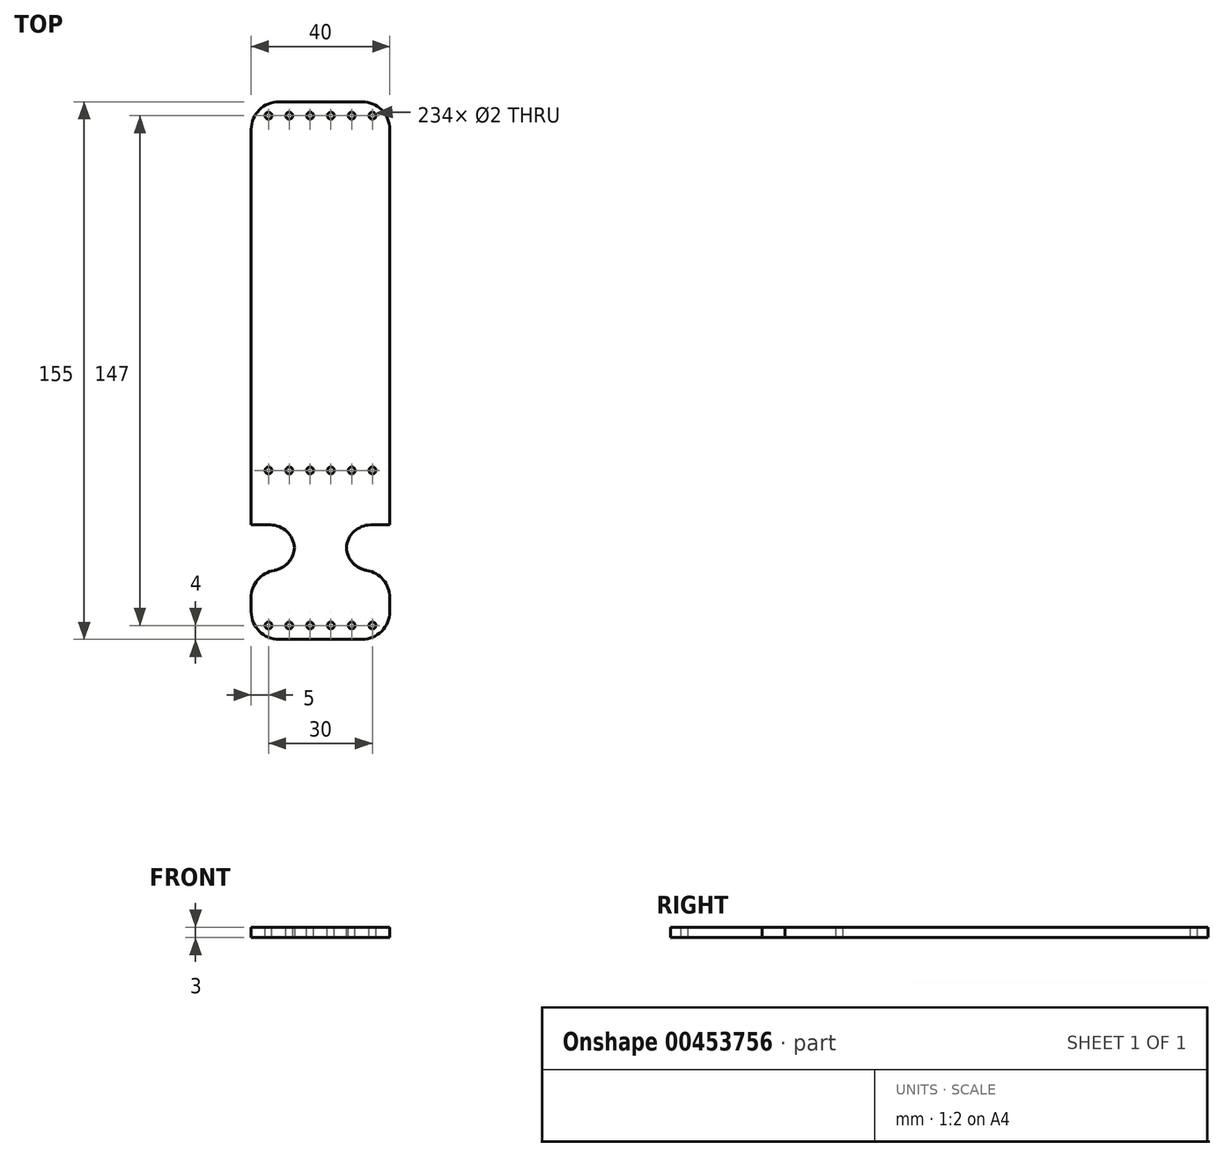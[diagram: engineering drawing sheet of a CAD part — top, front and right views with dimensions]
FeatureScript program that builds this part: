
annotation { "Feature Type Name" : "Feature", "Feature Type Description" : "" }
export const myFeature = defineFeature(function(context is Context, id is Id, definition is map)
    precondition{}
    {
        {
            var Q0;
            Q0=qCreatedBy(makeId("Top.planeOp"),FACE);
            var sketch = newSketch(context, id + "F0", { "sketchPlane" : qUnion([Q0])});
            skLineSegment(sketch, "E0.bottom", {"start": v(-20, 77.5) * mm, "end": v(20, 77.5) * mm});
            skLineSegment(sketch, "E0.top", {"start": v(-20, -77.5) * mm, "end": v(20, -77.5) * mm});
            skLineSegment(sketch, "E0.left", {"start": v(-20, 77.5) * mm, "end": v(-20, -77.5) * mm});
            skLineSegment(sketch, "E0.right", {"start": v(20, 77.5) * mm, "end": v(20, -77.5) * mm});
            skSolve(sketch);
        }
        {
            var Q0;
            Q0 = qSketchRegion(id + "F0", true);
            extrude(context, id + "F1", {"entities" : qUnion([Q0]), "depth" : 3 * mm});
        }
        {
            var Q0;
            Q0=makeQuery(id+"F1.opExtrude","CAP_FACE",FACE,{"disambiguationData":[OSD([sQuery(id+"F0.wireOp",EDGE,"E0.bottom"),sQuery(id+"F0.wireOp",EDGE,"E0.top"),sQuery(id+"F0.wireOp",EDGE,"E0.left"),sQuery(id+"F0.wireOp",EDGE,"E0.right")])],"isStart":false});
            var sketch = newSketch(context, id + "F2", { "sketchPlane" : qUnion([Q0])});
            skLineSegment(sketch, "E1.bottom", {"start": v(-20, -57.5) * mm, "end": v(20, -57.5) * mm});
            skLineSegment(sketch, "E1.top", {"start": v(-20, -44.5) * mm, "end": v(20, -44.5) * mm});
            skLineSegment(sketch, "E1.left", {"start": v(-20, -57.5) * mm, "end": v(-20, -44.5) * mm});
            skLineSegment(sketch, "E1.right", {"start": v(20, -57.5) * mm, "end": v(20, -44.5) * mm});
            skLineSegment(sketch, "E2.bottom", {"start": v(-7.5, -44.5) * mm, "end": v(7.5, -44.5) * mm});
            skLineSegment(sketch, "E2.top", {"start": v(-7.5, -57.5) * mm, "end": v(7.5, -57.5) * mm});
            skLineSegment(sketch, "E2.left", {"start": v(-7.5, -44.5) * mm, "end": v(-7.5, -57.5) * mm});
            skLineSegment(sketch, "E2.right", {"start": v(7.5, -44.5) * mm, "end": v(7.5, -57.5) * mm});
            skSolve(sketch);
        }
        {
            var Q0;
            {var subQ0=sQuery(id+"F2.wireOp",EDGE,"E1.left");Q0=makeQuery(id+"F2.imprint","IMPRINT",FACE,{"disambiguationData":[TD([[makeQuery(id+"F2.imprint","IMPRINT",EDGE,{"derivedFrom":subQ0}),1.0]])]});}
            var Q1;
            {var subQ0=sQuery(id+"F2.wireOp",EDGE,"E1.right");Q1=makeQuery(id+"F2.imprint","IMPRINT",FACE,{"disambiguationData":[TD([[makeQuery(id+"F2.imprint","IMPRINT",EDGE,{"derivedFrom":subQ0}),-1.0]])]});}
            extrude(context, id + "F3", {"entities" : qUnion([Q0, Q1]), "operationType" : NewBodyOperationType.REMOVE, "endBound" : BoundingType.UP_TO_NEXT, "oppositeDirection" : true, "depth" : 25 * mm});
        }
        {
            var Q0;
            Q0=makeQuery(id+"F3.boolean.opBoolean","COPY",EDGE,{"derivedFrom":makeQuery(id+"F3.opExtrude","SWEPT_EDGE",EDGE,{"disambiguationData":[OSD([sQuery(id+"F0.wireOp",EDGE,"E0.left"),sQuery(id+"F2.wireOp",EDGE,"E1.top"),sQuery(id+"F2.wireOp",EDGE,"E1.left")])]})});
            var Q1;
            Q1=makeQuery(id+"F3.boolean.opBoolean","COPY",EDGE,{"derivedFrom":makeQuery(id+"F3.opExtrude","SWEPT_EDGE",EDGE,{"disambiguationData":[OSD([sQuery(id+"F0.wireOp",EDGE,"E0.right"),sQuery(id+"F2.wireOp",EDGE,"E1.top"),sQuery(id+"F2.wireOp",EDGE,"E1.right")])]})});
            var Q2;
            Q2=makeQuery(id+"F3.boolean.opBoolean","COPY",EDGE,{"derivedFrom":makeQuery(id+"F3.opExtrude","SWEPT_EDGE",EDGE,{"disambiguationData":[OSD([sQuery(id+"F0.wireOp",EDGE,"E0.right"),sQuery(id+"F2.wireOp",EDGE,"E1.bottom"),sQuery(id+"F2.wireOp",EDGE,"E1.right")])]})});
            var Q3;
            Q3=makeQuery(id+"F3.boolean.opBoolean","COPY",EDGE,{"derivedFrom":makeQuery(id+"F3.opExtrude","SWEPT_EDGE",EDGE,{"disambiguationData":[OSD([sQuery(id+"F0.wireOp",EDGE,"E0.left"),sQuery(id+"F2.wireOp",EDGE,"E1.bottom"),sQuery(id+"F2.wireOp",EDGE,"E1.left")])]})});
            var Q4;
            Q4=makeQuery(id+"F1.opExtrude","SWEPT_EDGE",EDGE,{"disambiguationData":[OSD([sQuery(id+"F0.wireOp",EDGE,"E0.top"),sQuery(id+"F0.wireOp",EDGE,"E0.left")])]});
            var Q5;
            Q5=makeQuery(id+"F1.opExtrude","SWEPT_EDGE",EDGE,{"disambiguationData":[OSD([sQuery(id+"F0.wireOp",EDGE,"E0.top"),sQuery(id+"F0.wireOp",EDGE,"E0.right")])]});
            var Q6;
            Q6=makeQuery(id+"F1.opExtrude","SWEPT_EDGE",EDGE,{"disambiguationData":[OSD([sQuery(id+"F0.wireOp",EDGE,"E0.bottom"),sQuery(id+"F0.wireOp",EDGE,"E0.left")])]});
            var Q7;
            Q7=makeQuery(id+"F1.opExtrude","SWEPT_EDGE",EDGE,{"disambiguationData":[OSD([sQuery(id+"F0.wireOp",EDGE,"E0.bottom"),sQuery(id+"F0.wireOp",EDGE,"E0.right")])]});
            fillet(context, id + "F4", {"entities" : qUnion([Q0, Q1, Q2, Q3, Q4, Q5, Q6, Q7]), "radius" : 8 * mm, "tangentPropagation" : true, "allowEdgeOverflow" : false});
        }
        {
            var Q0;
            Q0=makeQuery(id+"F3.boolean.opBoolean","COPY",EDGE,{"derivedFrom":makeQuery(id+"F3.opExtrude","SWEPT_EDGE",EDGE,{"disambiguationData":[OSD([sQuery(id+"F2.wireOp",EDGE,"E1.top"),sQuery(id+"F2.wireOp",EDGE,"E2.bottom"),sQuery(id+"F2.wireOp",EDGE,"E2.left")])]})});
            var Q1;
            Q1=makeQuery(id+"F3.boolean.opBoolean","COPY",EDGE,{"derivedFrom":makeQuery(id+"F3.opExtrude","SWEPT_EDGE",EDGE,{"disambiguationData":[OSD([sQuery(id+"F2.wireOp",EDGE,"E1.bottom"),sQuery(id+"F2.wireOp",EDGE,"E2.top"),sQuery(id+"F2.wireOp",EDGE,"E2.left")])]})});
            var Q2;
            Q2=makeQuery(id+"F3.boolean.opBoolean","COPY",EDGE,{"derivedFrom":makeQuery(id+"F3.opExtrude","SWEPT_EDGE",EDGE,{"disambiguationData":[OSD([sQuery(id+"F2.wireOp",EDGE,"E1.top"),sQuery(id+"F2.wireOp",EDGE,"E2.bottom"),sQuery(id+"F2.wireOp",EDGE,"E2.right")])]})});
            var Q3;
            Q3=makeQuery(id+"F3.boolean.opBoolean","COPY",EDGE,{"derivedFrom":makeQuery(id+"F3.opExtrude","SWEPT_EDGE",EDGE,{"disambiguationData":[OSD([sQuery(id+"F2.wireOp",EDGE,"E1.bottom"),sQuery(id+"F2.wireOp",EDGE,"E2.top"),sQuery(id+"F2.wireOp",EDGE,"E2.right")])]})});
            fillet(context, id + "F5", {"entities" : qUnion([Q0, Q1, Q2, Q3]), "radius" : 7 * mm, "tangentPropagation" : true, "allowEdgeOverflow" : false});
        }
        {
            var Q0;
            Q0=makeQuery(id+"F1.opExtrude","CAP_FACE",FACE,{"disambiguationData":[OSD([sQuery(id+"F0.wireOp",EDGE,"E0.bottom"),sQuery(id+"F0.wireOp",EDGE,"E0.top"),sQuery(id+"F0.wireOp",EDGE,"E0.left"),sQuery(id+"F0.wireOp",EDGE,"E0.right")])],"isStart":false});
            var sketch = newSketch(context, id + "F6", { "sketchPlane" : qUnion([Q0])});
            skCircle(sketch, "E3", {"center": v(-15, -73.5) * mm, "radius": 1 * mm});
            skCircle(sketch, "E4.1.0.0", {"center": v(-9, -73.5) * mm, "radius": 1 * mm});
            skCircle(sketch, "E4.2.0.0", {"center": v(-3, -73.5) * mm, "radius": 1 * mm});
            skCircle(sketch, "E4.3.0.0", {"center": v(3, -73.5) * mm, "radius": 1 * mm});
            skLineSegment(sketch, "E4.direction1", {"start": v(-15, -73.5) * mm, "end": v(-9, -73.5) * mm, "construction": true});
            skCircle(sketch, "E5", {"center": v(-15, -28.8) * mm, "radius": 1 * mm});
            skCircle(sketch, "E6.1.0.0", {"center": v(-9, -28.8) * mm, "radius": 1 * mm});
            skCircle(sketch, "E6.2.0.0", {"center": v(-3, -28.8) * mm, "radius": 1 * mm});
            skCircle(sketch, "E6.3.0.0", {"center": v(3, -28.8) * mm, "radius": 1 * mm});
            skLineSegment(sketch, "E6.direction1", {"start": v(-15, -28.8) * mm, "end": v(-9, -28.8) * mm, "construction": true});
            skCircle(sketch, "E7", {"center": v(-15, 73.5) * mm, "radius": 1 * mm});
            skCircle(sketch, "E8.1.0.0", {"center": v(-9, 73.5) * mm, "radius": 1 * mm});
            skCircle(sketch, "E8.2.0.0", {"center": v(-3, 73.5) * mm, "radius": 1 * mm});
            skCircle(sketch, "E8.3.0.0", {"center": v(3, 73.5) * mm, "radius": 1 * mm});
            skLineSegment(sketch, "E8.direction1", {"start": v(-15, 73.5) * mm, "end": v(-9, 73.5) * mm, "construction": true});
            skCircle(sketch, "E9.0.4.0", {"center": v(9, -73.5) * mm, "radius": 1 * mm});
            skCircle(sketch, "E9.0.5.0", {"center": v(15, -73.5) * mm, "radius": 1 * mm});
            skCircle(sketch, "E10.0.4.0", {"center": v(9, -28.8) * mm, "radius": 1 * mm});
            skCircle(sketch, "E10.0.5.0", {"center": v(15, -28.8) * mm, "radius": 1 * mm});
            skCircle(sketch, "E11.0.4.0", {"center": v(9, 73.5) * mm, "radius": 1 * mm});
            skCircle(sketch, "E11.0.5.0", {"center": v(15, 73.5) * mm, "radius": 1 * mm});
            skSolve(sketch);
        }
        {
            var Q0;
            Q0 = qSketchRegion(id + "F6", true);
            extrude(context, id + "F7", {"entities" : qUnion([Q0]), "operationType" : NewBodyOperationType.REMOVE, "endBound" : BoundingType.UP_TO_NEXT, "oppositeDirection" : true, "depth" : 25 * mm});
        }
    });
